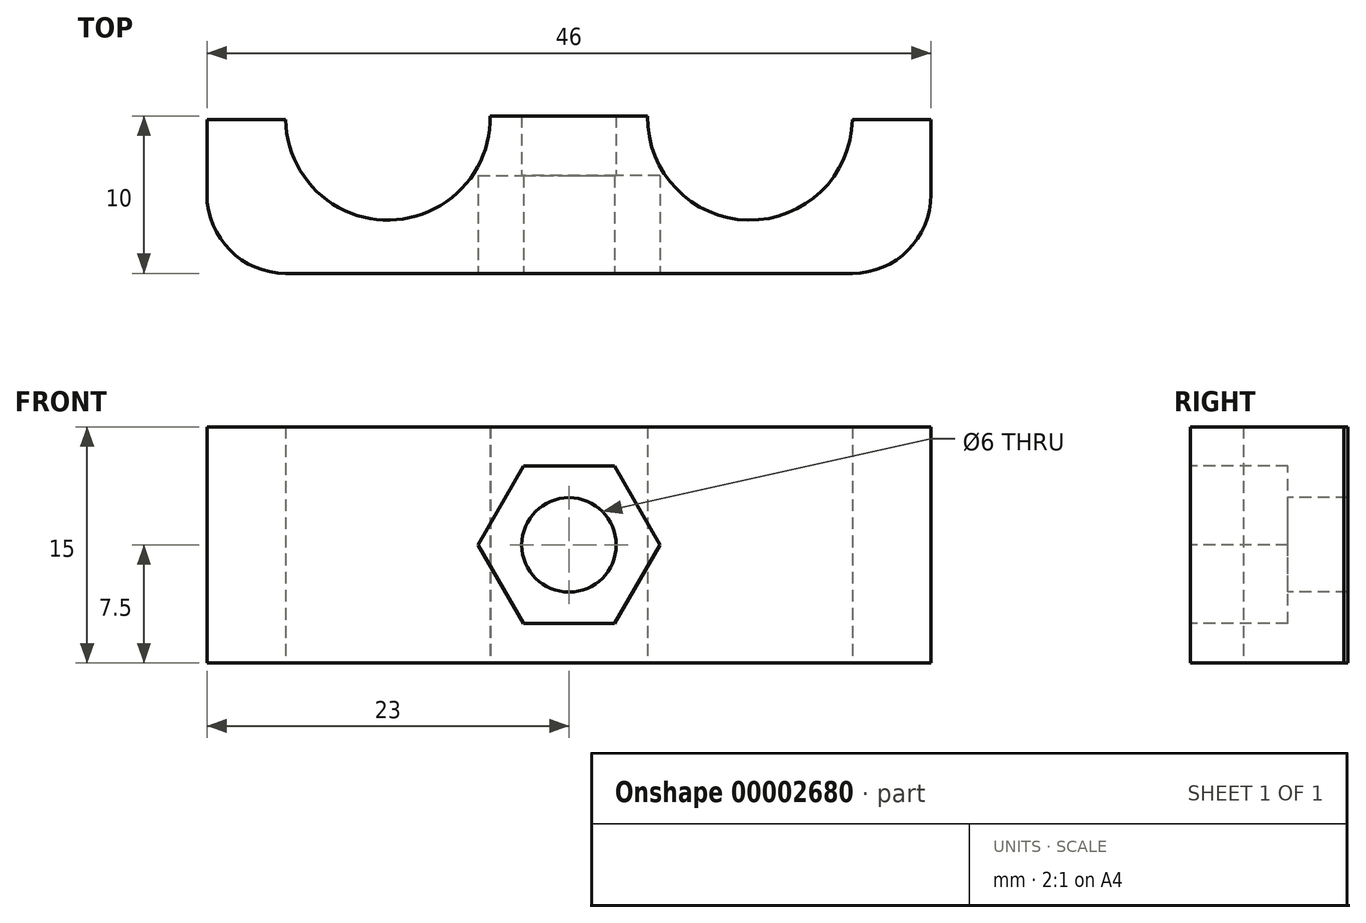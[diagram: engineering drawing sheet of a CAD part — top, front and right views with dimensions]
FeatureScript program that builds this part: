
annotation { "Feature Type Name" : "Feature", "Feature Type Description" : "" }
export const myFeature = defineFeature(function(context is Context, id is Id, definition is map)
    precondition{}
    {
        {
            var Q0;
            Q0=qCreatedBy(makeId("Top.planeOp"),FACE);
            var sketch = newSketch(context, id + "F0", { "sketchPlane" : qUnion([Q0])});
            skArc(sketch, "E0", {"start": v(-18.45, 22.31) * mm, "mid": v(-12.07, 15.7) * mm, "end": v(-5.45, 22.07) * mm});
            skLineSegment(sketch, "E1", {"start": v(-18.45, 22.31) * mm, "end": v(-23.45, 22.31) * mm});
            skLineSegment(sketch, "E2", {"start": v(-23.45, 12.31) * mm, "end": v(-5.45, 12.31) * mm});
            skLineSegment(sketch, "E3", {"start": v(-0.45, 17.31) * mm, "end": v(-0.45, 22.07) * mm});
            skPoint(sketch, "E4.visualSharp", {"position": v(-0.45, 12.31) * mm});
            skArc(sketch, "E4.filletArc", {"start": v(-5.45, 12.31) * mm, "mid": v(-1.92, 13.78) * mm, "end": v(-0.45, 17.31) * mm});
            skLineSegment(sketch, "E5", {"start": v(-5.45, 22.07) * mm, "end": v(-0.45, 22.07) * mm});
            skArc(sketch, "E6.MirrorCS", {"start": v(-28.45, 22.31) * mm, "mid": v(-34.83, 15.7) * mm, "end": v(-41.45, 22.07) * mm});
            skLineSegment(sketch, "E7.MirrorCS", {"start": v(-28.45, 22.31) * mm, "end": v(-23.45, 22.31) * mm});
            skLineSegment(sketch, "E8.MirrorCS", {"start": v(-23.45, 12.31) * mm, "end": v(-41.45, 12.31) * mm});
            skArc(sketch, "E9.MirrorCS", {"start": v(-41.45, 12.31) * mm, "mid": v(-44.98, 13.78) * mm, "end": v(-46.45, 17.31) * mm});
            skLineSegment(sketch, "E10.MirrorCS", {"start": v(-46.45, 17.31) * mm, "end": v(-46.45, 22.07) * mm});
            skLineSegment(sketch, "E11.MirrorCS", {"start": v(-41.45, 22.07) * mm, "end": v(-46.45, 22.07) * mm});
            skSolve(sketch);
        }
        {
            var Q0;
            Q0=makeQuery(id+"F0.imprint","IMPRINT",FACE,{"disambiguationData":[TD([[makeQuery(id+"F0.imprint","IMPRINT",EDGE,{"derivedFrom":sQuery(id+"F0.wireOp",EDGE,"E0")}),-1.0]])]});
            extrude(context, id + "F1", {"entities" : qUnion([Q0]), "depth" : 15 * mm});
        }
        {
            var Q0;
            Q0=makeQuery(id+"F1.opExtrude","SWEPT_FACE",FACE,{"disambiguationData":[OSD([sQuery(id+"F0.wireOp",EDGE,"E2"),sQuery(id+"F0.wireOp",EDGE,"E8.MirrorCS")])]});
            var sketch = newSketch(context, id + "F2", { "sketchPlane" : qUnion([Q0])});
            skLineSegment(sketch, "E12", {"start": v(-23.45, 15) * mm, "end": v(-23.45, 0) * mm});
            skCircle(sketch, "E13", {"center": v(-23.45, 7.5) * mm, "radius": 3 * mm});
            skCircle(sketch, "E14.cCircle", {"center": v(-23.45, 7.5) * mm, "radius": 5 * mm, "construction": true});
            skLineSegment(sketch, "E14.0", {"start": v(-26.34, 12.5) * mm, "end": v(-20.56, 12.5) * mm});
            skLineSegment(sketch, "E14.1", {"start": v(-20.56, 12.5) * mm, "end": v(-17.68, 7.5) * mm});
            skLineSegment(sketch, "E14.2", {"start": v(-17.68, 7.5) * mm, "end": v(-20.56, 2.5) * mm});
            skLineSegment(sketch, "E14.3", {"start": v(-20.56, 2.5) * mm, "end": v(-26.34, 2.5) * mm});
            skLineSegment(sketch, "E14.4", {"start": v(-26.34, 2.5) * mm, "end": v(-29.22, 7.5) * mm});
            skLineSegment(sketch, "E14.5", {"start": v(-29.22, 7.5) * mm, "end": v(-26.34, 12.5) * mm});
            skPoint(sketch, "E14.0.midPoint", {"position": v(-23.45, 12.5) * mm});
            skSolve(sketch);
        }
        {
            var Q0;
            {var subQ0=sQuery(id+"F2.wireOp",EDGE,"E13");var subQ1=sQuery(id+"F2.wireOp",EDGE,"E12");var subQ2=makeQuery(id+"F2.imprint","INTERSECT",VERTEX,{"disambiguationData":[OD(0.0)],"derivedFrom":[subQ1,subQ0]});Q0=makeQuery(id+"F2.imprint","IMPRINT",FACE,{"disambiguationData":[TD([[makeQuery(id+"F2.imprint","IMPRINT",EDGE,{"disambiguationData":[TD([[subQ2,-1.0]])],"derivedFrom":subQ1}),1.0]])]});}
            var Q1;
            {var subQ0=sQuery(id+"F2.wireOp",EDGE,"E13");var subQ1=sQuery(id+"F2.wireOp",EDGE,"E12");var subQ2=makeQuery(id+"F2.imprint","INTERSECT",VERTEX,{"disambiguationData":[OD(0.0)],"derivedFrom":[subQ1,subQ0]});Q1=makeQuery(id+"F2.imprint","IMPRINT",FACE,{"disambiguationData":[TD([[makeQuery(id+"F2.imprint","IMPRINT",EDGE,{"disambiguationData":[TD([[subQ2,-1.0]])],"derivedFrom":subQ1}),-1.0]])]});}
            extrude(context, id + "F3", {"entities" : qUnion([Q0, Q1]), "operationType" : NewBodyOperationType.REMOVE, "oppositeDirection" : true, "depth" : 25 * mm});
        }
        {
            var Q0;
            Q0=qSketchRegion(id+"F2",true);
            extrude(context, id + "F4", {"entities" : qUnion([Q0]), "operationType" : NewBodyOperationType.REMOVE, "oppositeDirection" : true, "depth" : 6.2 * mm});
        }
    });
